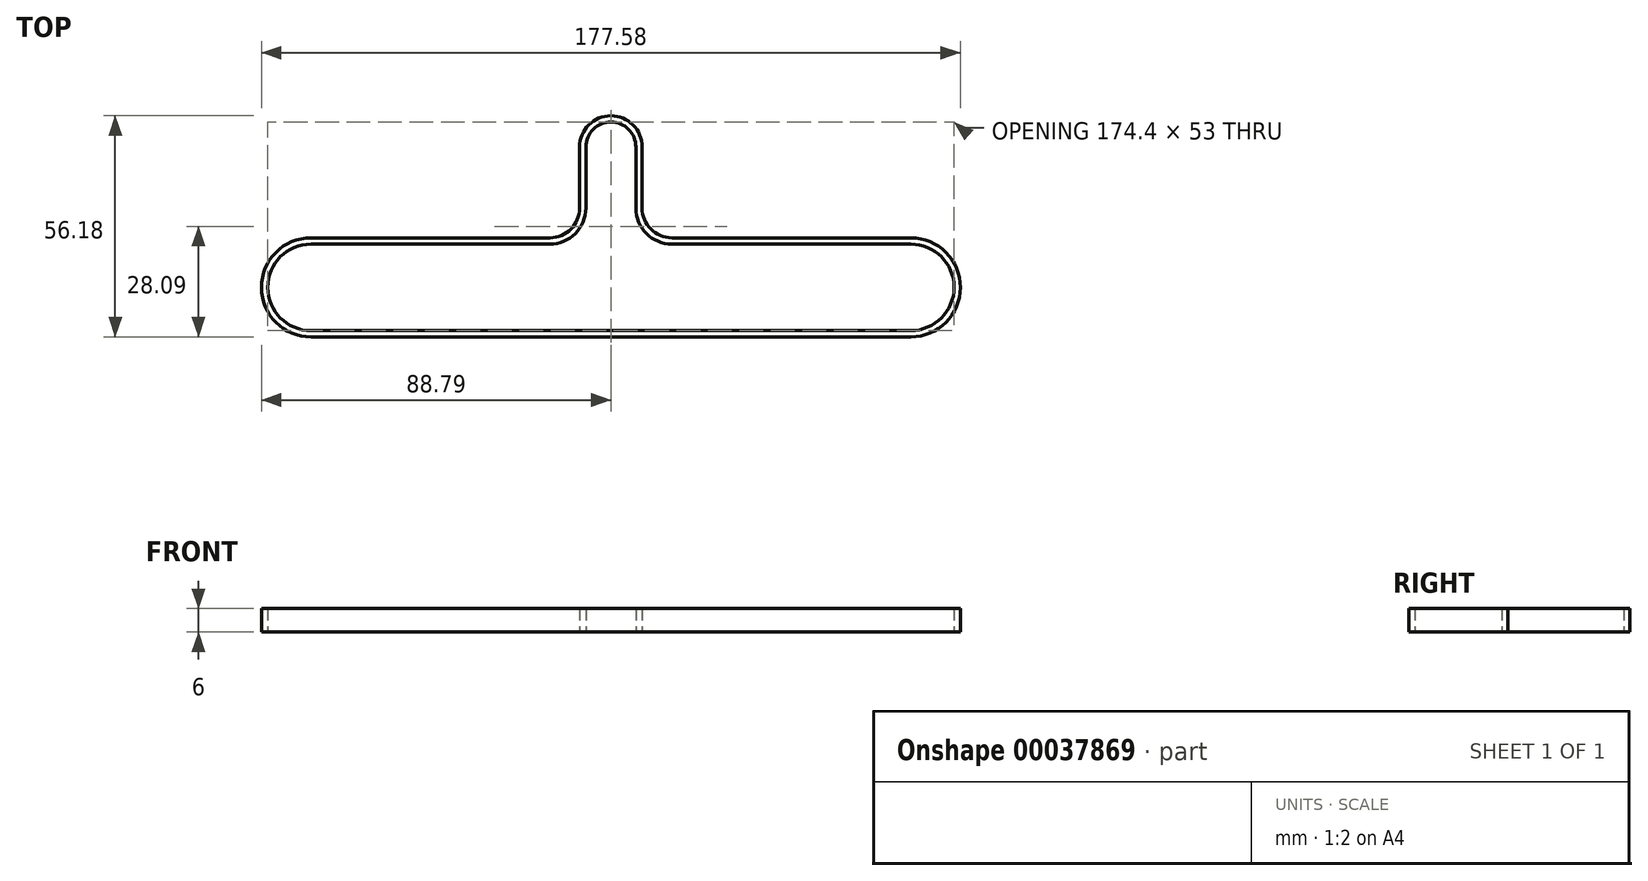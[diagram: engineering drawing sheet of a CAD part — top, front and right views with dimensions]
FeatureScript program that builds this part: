
annotation { "Feature Type Name" : "Feature", "Feature Type Description" : "" }
export const myFeature = defineFeature(function(context is Context, id is Id, definition is map)
    precondition{}
    {
        {
            var Q0;
            Q0=qCreatedBy(makeId("Top.planeOp"),FACE);
            var sketch = newSketch(context, id + "F0", { "sketchPlane" : qUnion([Q0])});
            skLineSegment(sketch, "E0", {"start": v(0, 0) * mm, "end": v(0, -15.5) * mm, "construction": true});
            skLineSegment(sketch, "E1", {"start": v(-76.2, -35.65) * mm, "end": v(76.2, -35.65) * mm, "construction": true});
            skLineSegment(sketch, "E2", {"start": v(76.2, -24.65) * mm, "end": v(76.2, -46.65) * mm, "construction": true});
            skLineSegment(sketch, "E3", {"start": v(-76.2, -24.65) * mm, "end": v(-76.2, -46.65) * mm, "construction": true});
            skLineSegment(sketch, "E4", {"start": v(15.5, -23.06) * mm, "end": v(15.5, -24.65) * mm, "construction": true});
            skLineSegment(sketch, "E5", {"start": v(76.2, -24.65) * mm, "end": v(76.2, -23.06) * mm, "construction": true});
            skLineSegment(sketch, "E6", {"start": v(76.2, -46.65) * mm, "end": v(76.2, -48.24) * mm, "construction": true});
            skLineSegment(sketch, "E7", {"start": v(-76.2, -46.65) * mm, "end": v(-76.2, -48.24) * mm, "construction": true});
            skLineSegment(sketch, "E8", {"start": v(-76.2, -24.65) * mm, "end": v(-76.2, -23.06) * mm, "construction": true});
            skArc(sketch, "E9", {"start": v(7.94, -15.5) * mm, "mid": v(10.15, -20.85) * mm, "end": v(15.5, -23.06) * mm});
            skArc(sketch, "E10", {"start": v(6.35, -15.5) * mm, "mid": v(9.03, -21.97) * mm, "end": v(15.5, -24.65) * mm});
            skLineSegment(sketch, "E11", {"start": v(15.5, -24.65) * mm, "end": v(76.2, -24.65) * mm});
            skLineSegment(sketch, "E12", {"start": v(15.5, -23.06) * mm, "end": v(76.2, -23.06) * mm});
            skLineSegment(sketch, "E13", {"start": v(6.35, -15.5) * mm, "end": v(6.35, 0) * mm});
            skLineSegment(sketch, "E14", {"start": v(7.94, -15.5) * mm, "end": v(7.94, 0) * mm});
            skLineSegment(sketch, "E15", {"start": v(-6.35, -15.5) * mm, "end": v(-6.35, 0) * mm});
            skArc(sketch, "E16", {"start": v(6.35, 0) * mm, "mid": v(0, 6.35) * mm, "end": v(-6.35, 0) * mm});
            skArc(sketch, "E17", {"start": v(7.94, 0) * mm, "mid": v(0, 7.94) * mm, "end": v(-7.94, 0) * mm});
            skLineSegment(sketch, "E18", {"start": v(-76.2, -24.65) * mm, "end": v(-15.5, -24.65) * mm});
            skLineSegment(sketch, "E19", {"start": v(-76.2, -46.65) * mm, "end": v(76.2, -46.65) * mm});
            skLineSegment(sketch, "E20", {"start": v(76.2, -48.24) * mm, "end": v(-76.2, -48.24) * mm});
            skLineSegment(sketch, "E21", {"start": v(-76.2, -23.06) * mm, "end": v(-15.5, -23.06) * mm});
            skArc(sketch, "E22", {"start": v(-15.5, -24.65) * mm, "mid": v(-9.03, -21.97) * mm, "end": v(-6.35, -15.5) * mm});
            skArc(sketch, "E23", {"start": v(-15.5, -23.06) * mm, "mid": v(-10.15, -20.85) * mm, "end": v(-7.94, -15.5) * mm});
            skLineSegment(sketch, "E24", {"start": v(-7.94, 0) * mm, "end": v(-7.94, -15.5) * mm});
            skLineSegment(sketch, "E25", {"start": v(-15.5, -24.65) * mm, "end": v(-15.5, -23.06) * mm, "construction": true});
            skArc(sketch, "E26", {"start": v(76.2, -48.24) * mm, "mid": v(88.79, -35.65) * mm, "end": v(76.2, -23.06) * mm});
            skArc(sketch, "E27", {"start": v(76.2, -46.65) * mm, "mid": v(87.2, -35.65) * mm, "end": v(76.2, -24.65) * mm});
            skArc(sketch, "E28", {"start": v(-76.2, -24.65) * mm, "mid": v(-87.2, -35.65) * mm, "end": v(-76.2, -46.65) * mm});
            skArc(sketch, "E29", {"start": v(-76.2, -23.06) * mm, "mid": v(-88.79, -35.65) * mm, "end": v(-76.2, -48.24) * mm});
            skLineSegment(sketch, "E30", {"start": v(-15.5, -15.5) * mm, "end": v(15.5, -15.5) * mm, "construction": true});
            skPoint(sketch, "E30.startSnap0", {"position": v(0, -7.75) * mm});
            skSolve(sketch);
        }
        {
            var Q0;
            Q0 = qSketchRegion(id + "F0", true);
            extrude(context, id + "F1", {"entities" : qUnion([Q0]), "depth" : 6 * mm});
        }
    });
